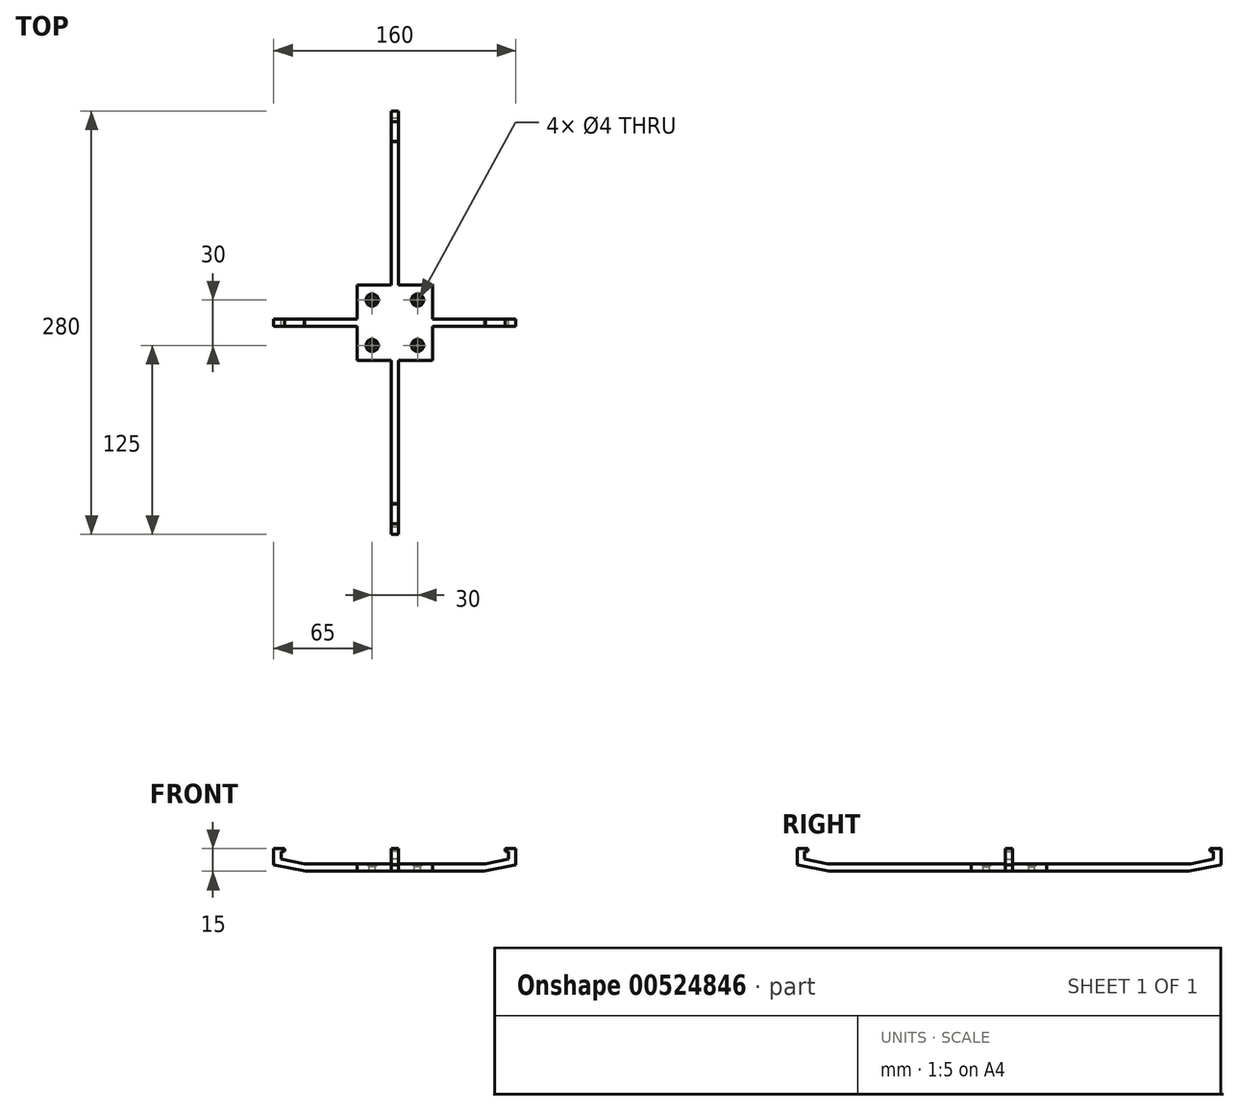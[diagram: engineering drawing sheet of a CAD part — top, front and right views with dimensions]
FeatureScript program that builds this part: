
annotation { "Feature Type Name" : "Feature", "Feature Type Description" : "" }
export const myFeature = defineFeature(function(context is Context, id is Id, definition is map)
    precondition{}
    {
        {
            var Q0;
            Q0=qCreatedBy(makeId("Front.planeOp"),FACE);
            var sketch = newSketch(context, id + "F0", { "sketchPlane" : qUnion([Q0])});
            skLineSegment(sketch, "E0", {"start": v(-75, 8) * mm, "end": v(-73, 8) * mm});
            skLineSegment(sketch, "E1", {"start": v(-73, 8) * mm, "end": v(-73, 10) * mm});
            skLineSegment(sketch, "E2", {"start": v(-73, 10) * mm, "end": v(-80, 10) * mm});
            skLineSegment(sketch, "E3", {"start": v(-80, 10) * mm, "end": v(-80, -0.8) * mm});
            skLineSegment(sketch, "E4", {"start": v(-80, -0.8) * mm, "end": v(-59, -5) * mm});
            skLineSegment(sketch, "E5", {"start": v(-59, -5) * mm, "end": v(59, -5) * mm});
            skLineSegment(sketch, "E6", {"start": v(59, -5) * mm, "end": v(80, -0.8) * mm});
            skLineSegment(sketch, "E7", {"start": v(80, -0.8) * mm, "end": v(80, 10) * mm});
            skLineSegment(sketch, "E8", {"start": v(80, 10) * mm, "end": v(73, 10) * mm});
            skLineSegment(sketch, "E9", {"start": v(73, 10) * mm, "end": v(73, 8) * mm});
            skLineSegment(sketch, "E10", {"start": v(73, 8) * mm, "end": v(75, 8) * mm});
            skLineSegment(sketch, "E11", {"start": v(75, 8) * mm, "end": v(75, 3) * mm});
            skLineSegment(sketch, "E12", {"start": v(75, 3) * mm, "end": v(60, 0) * mm});
            skLineSegment(sketch, "E13", {"start": v(60, 0) * mm, "end": v(-60, 0) * mm});
            skLineSegment(sketch, "E14", {"start": v(-60, 0) * mm, "end": v(-75, 3) * mm});
            skLineSegment(sketch, "E15", {"start": v(-75, 3) * mm, "end": v(-75, 8) * mm});
            skSolve(sketch);
        }
        {
            var Q0;
            Q0 = qSketchRegion(id + "F0", true);
            extrude(context, id + "F1", {"entities" : qUnion([Q0]), "endBound" : BoundingType.SYMMETRIC, "depth" : 5 * mm, "offsetDistance" : 25 * mm});
        }
        {
            var Q0;
            Q0=qCreatedBy(makeId("Right.planeOp"),FACE);
            var sketch = newSketch(context, id + "F2", { "sketchPlane" : qUnion([Q0])});
            skLineSegment(sketch, "E16", {"start": v(-135, 8) * mm, "end": v(-133, 8) * mm});
            skLineSegment(sketch, "E17", {"start": v(-133, 8) * mm, "end": v(-133, 10) * mm});
            skLineSegment(sketch, "E18", {"start": v(-133, 10) * mm, "end": v(-140, 10) * mm});
            skLineSegment(sketch, "E19", {"start": v(-140, 10) * mm, "end": v(-140, -0.8) * mm});
            skLineSegment(sketch, "E20", {"start": v(-140, -0.8) * mm, "end": v(-119, -5) * mm});
            skLineSegment(sketch, "E21", {"start": v(-119, -5) * mm, "end": v(119, -5) * mm});
            skLineSegment(sketch, "E22", {"start": v(119, -5) * mm, "end": v(140, -0.8) * mm});
            skLineSegment(sketch, "E23", {"start": v(140, -0.8) * mm, "end": v(140, 10) * mm});
            skLineSegment(sketch, "E24", {"start": v(140, 10) * mm, "end": v(133, 10) * mm});
            skLineSegment(sketch, "E25", {"start": v(133, 10) * mm, "end": v(133, 8) * mm});
            skLineSegment(sketch, "E26", {"start": v(133, 8) * mm, "end": v(135, 8) * mm});
            skLineSegment(sketch, "E27", {"start": v(135, 8) * mm, "end": v(135, 3) * mm});
            skLineSegment(sketch, "E28", {"start": v(135, 3) * mm, "end": v(120, 0) * mm});
            skLineSegment(sketch, "E29", {"start": v(120, 0) * mm, "end": v(-120, 0) * mm});
            skLineSegment(sketch, "E30", {"start": v(-120, 0) * mm, "end": v(-135, 3) * mm});
            skLineSegment(sketch, "E31", {"start": v(-135, 3) * mm, "end": v(-135, 8) * mm});
            skSolve(sketch);
        }
        {
            var Q0;
            Q0 = qSketchRegion(id + "F2", true);
            var Q1;
            Q1 = qConstructionFilter(qBodyType(qCreatedBy(id + "F2" ,EDGE), BodyType.WIRE), ConstructionObject.NO);
            extrude(context, id + "F3", {"entities" : qUnion([Q0]), "operationType" : NewBodyOperationType.ADD, "surfaceEntities" : qUnion([Q1]), "endBound" : BoundingType.SYMMETRIC, "depth" : 5 * mm, "offsetDistance" : 25 * mm});
        }
        {
            var Q0;
            Q0=qCreatedBy(makeId("Top.planeOp"),FACE);
            var sketch = newSketch(context, id + "F4", { "sketchPlane" : qUnion([Q0])});
            skLineSegment(sketch, "E32.bottom", {"start": v(-25, 25) * mm, "end": v(25, 25) * mm});
            skLineSegment(sketch, "E32.top", {"start": v(-25, -25) * mm, "end": v(25, -25) * mm});
            skLineSegment(sketch, "E32.left", {"start": v(-25, 25) * mm, "end": v(-25, -25) * mm});
            skLineSegment(sketch, "E32.right", {"start": v(25, 25) * mm, "end": v(25, -25) * mm});
            skSolve(sketch);
        }
        {
            var Q0;
            Q0 = qSketchRegion(id + "F4", true);
            extrude(context, id + "F5", {"entities" : qUnion([Q0]), "operationType" : NewBodyOperationType.ADD, "oppositeDirection" : true, "depth" : 5 * mm, "offsetDistance" : 25 * mm});
        }
        {
            var Q0;
            Q0=makeQuery(id+"F5.boolean.opBoolean","MERGE",FACE,{"derivedFrom":[makeQuery(id+"F3.boolean.opBoolean","MERGE",FACE,{"derivedFrom":[makeQuery(id+"F1.opExtrude","SWEPT_FACE",FACE,{"disambiguationData":[OSD([sQuery(id+"F0.wireOp",EDGE,"E13")])]}),makeQuery(id+"F3.opExtrude","SWEPT_FACE",FACE,{"disambiguationData":[OSD([sQuery(id+"F2.wireOp",EDGE,"E29")])]})]}),makeQuery(id+"F5.opExtrude","CAP_FACE",FACE,{"disambiguationData":[OSD([sQuery(id+"F4.wireOp",EDGE,"E32.bottom"),sQuery(id+"F4.wireOp",EDGE,"E32.top"),sQuery(id+"F4.wireOp",EDGE,"E32.left"),sQuery(id+"F4.wireOp",EDGE,"E32.right")])],"isStart":true})]});
            var sketch = newSketch(context, id + "F6", { "sketchPlane" : qUnion([Q0])});
            skPoint(sketch, "E33", {"position": v(-15, 15) * mm});
            skPoint(sketch, "E34", {"position": v(15, 15) * mm});
            skPoint(sketch, "E35", {"position": v(15, -15) * mm});
            skPoint(sketch, "E36", {"position": v(-15, -15) * mm});
            skSolve(sketch);
        }
        {
            var Q0;
            Q0=sQuery(id+"F6.wireOp",VERTEX,"E35");
            var Q1;
            Q1=sQuery(id+"F6.wireOp",VERTEX,"E36");
            var Q2;
            Q2=sQuery(id+"F6.wireOp",VERTEX,"E33");
            var Q3;
            Q3=sQuery(id+"F6.wireOp",VERTEX,"E34");
            var Q4;
            Q4=makeQuery(id+"F1.opExtrude","SWEPT_BODY",BODY,{"disambiguationData":[OSD([sQuery(id+"F0.wireOp",EDGE,"E0"),sQuery(id+"F0.wireOp",EDGE,"E1"),sQuery(id+"F0.wireOp",EDGE,"E2"),sQuery(id+"F0.wireOp",EDGE,"E3"),sQuery(id+"F0.wireOp",EDGE,"E4"),sQuery(id+"F0.wireOp",EDGE,"E5"),sQuery(id+"F0.wireOp",EDGE,"E6"),sQuery(id+"F0.wireOp",EDGE,"E7"),sQuery(id+"F0.wireOp",EDGE,"E8"),sQuery(id+"F0.wireOp",EDGE,"E9"),sQuery(id+"F0.wireOp",EDGE,"E10"),sQuery(id+"F0.wireOp",EDGE,"E11"),sQuery(id+"F0.wireOp",EDGE,"E12"),sQuery(id+"F0.wireOp",EDGE,"E13"),sQuery(id+"F0.wireOp",EDGE,"E14"),sQuery(id+"F0.wireOp",EDGE,"E15")])]});
            hole(context, id + "F7", {"style" : HoleStyle.C_SINK, "endStyle" : HoleEndStyle.THROUGH, "holeDiameter" : 4 * mm, "cSinkDiameter" : 8 * mm, "cSinkAngle" : 90 * degree, "isTappedThrough" : true, "tappedDepth" : 12 * mm, "tapClearance" : 3, "locations" : qUnion([Q0, Q1, Q2, Q3]), "scope" : qUnion([Q4])});
        }
    });
